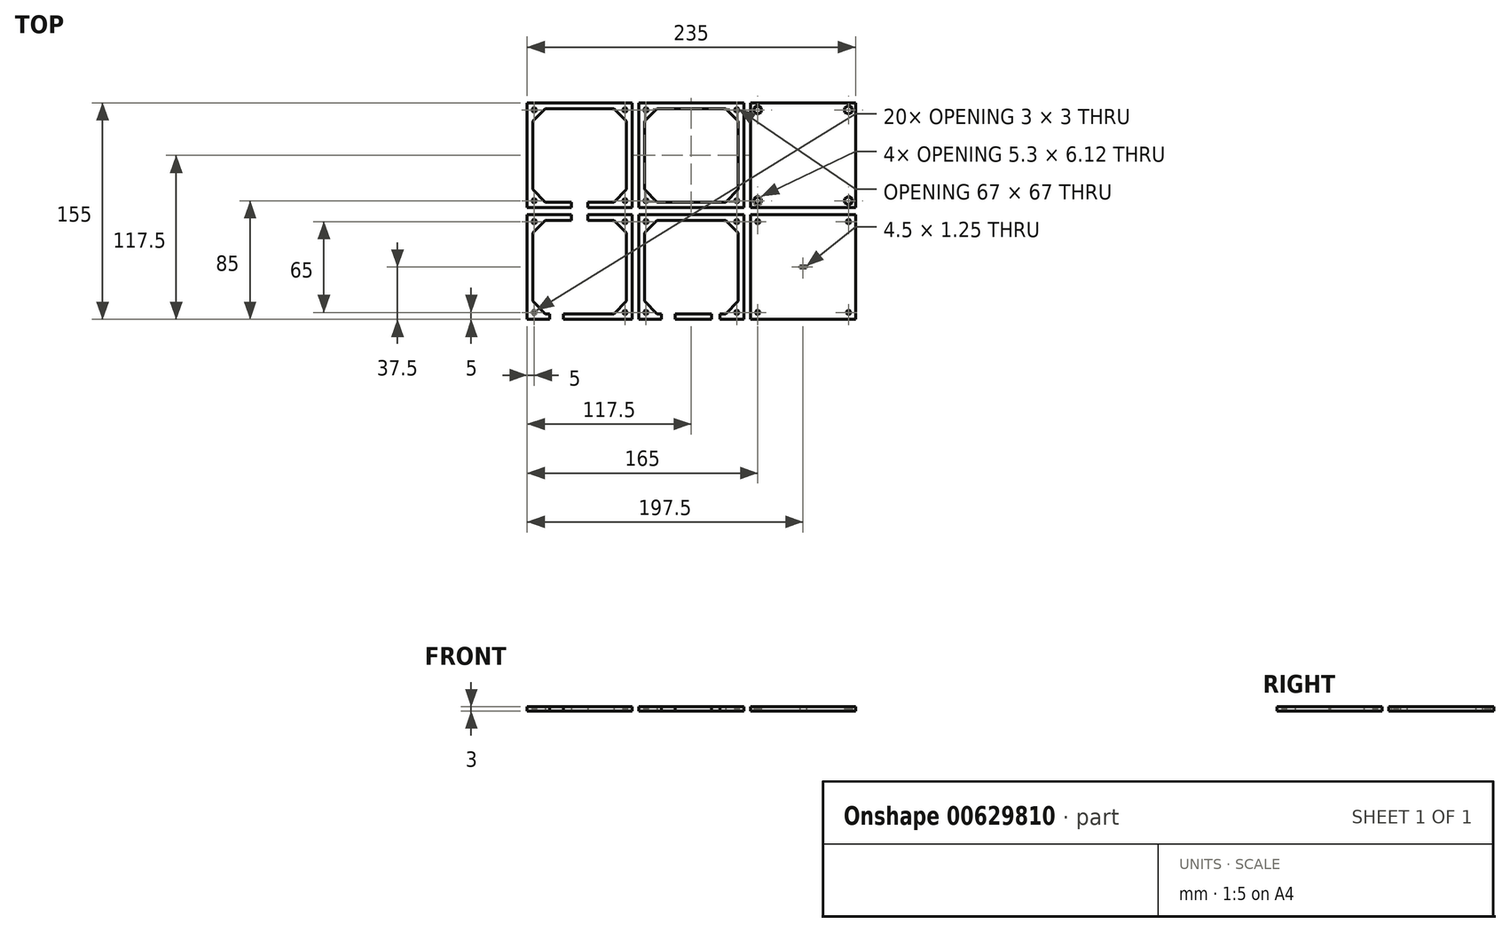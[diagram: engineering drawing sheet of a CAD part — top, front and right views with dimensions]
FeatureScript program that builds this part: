
annotation { "Feature Type Name" : "Feature", "Feature Type Description" : "" }
export const myFeature = defineFeature(function(context is Context, id is Id, definition is map)
    precondition{}
    {
        {
            var Q0;
            Q0=qCreatedBy(makeId("Top.planeOp"),FACE);
            var sketch = newSketch(context, id + "F0", { "sketchPlane" : qUnion([Q0])});
            skLineSegment(sketch, "E0", {"start": v(-111.29, 73.38) * mm, "end": v(-111.62, 73.71) * mm});
            skLineSegment(sketch, "E1", {"start": v(-111.62, 73.71) * mm, "end": v(-112.04, 73.93) * mm});
            skLineSegment(sketch, "E2", {"start": v(-112.04, 73.93) * mm, "end": v(-112.5, 74) * mm});
            skLineSegment(sketch, "E3", {"start": v(-112.5, 74) * mm, "end": v(-112.96, 73.93) * mm});
            skLineSegment(sketch, "E4", {"start": v(-112.96, 73.93) * mm, "end": v(-113.38, 73.71) * mm});
            skLineSegment(sketch, "E5", {"start": v(-113.38, 73.71) * mm, "end": v(-113.71, 73.38) * mm});
            skLineSegment(sketch, "E6", {"start": v(-113.71, 73.38) * mm, "end": v(-113.93, 72.96) * mm});
            skLineSegment(sketch, "E7", {"start": v(-113.93, 72.96) * mm, "end": v(-114, 72.5) * mm});
            skLineSegment(sketch, "E8", {"start": v(-114, 72.5) * mm, "end": v(-113.93, 72.04) * mm});
            skLineSegment(sketch, "E9", {"start": v(-113.93, 72.04) * mm, "end": v(-113.71, 71.62) * mm});
            skLineSegment(sketch, "E10", {"start": v(-113.71, 71.62) * mm, "end": v(-113.38, 71.29) * mm});
            skLineSegment(sketch, "E11", {"start": v(-113.38, 71.29) * mm, "end": v(-112.96, 71.07) * mm});
            skLineSegment(sketch, "E12", {"start": v(-112.96, 71.07) * mm, "end": v(-112.5, 71) * mm});
            skLineSegment(sketch, "E13", {"start": v(-112.5, 71) * mm, "end": v(-112.04, 71.07) * mm});
            skLineSegment(sketch, "E14", {"start": v(-112.04, 71.07) * mm, "end": v(-111.62, 71.29) * mm});
            skLineSegment(sketch, "E15", {"start": v(-111.62, 71.29) * mm, "end": v(-111.29, 71.62) * mm});
            skLineSegment(sketch, "E16", {"start": v(-111.29, 71.62) * mm, "end": v(-111.07, 72.04) * mm});
            skLineSegment(sketch, "E17", {"start": v(-111.07, 72.04) * mm, "end": v(-111, 72.5) * mm});
            skLineSegment(sketch, "E18", {"start": v(-111, 72.5) * mm, "end": v(-111.07, 72.96) * mm});
            skLineSegment(sketch, "E19", {"start": v(-46.07, 72.96) * mm, "end": v(-46.29, 73.38) * mm});
            skLineSegment(sketch, "E20", {"start": v(-46.29, 73.38) * mm, "end": v(-46.62, 73.71) * mm});
            skLineSegment(sketch, "E21", {"start": v(-46.62, 73.71) * mm, "end": v(-47.04, 73.93) * mm});
            skLineSegment(sketch, "E22", {"start": v(-47.04, 73.93) * mm, "end": v(-47.5, 74) * mm});
            skLineSegment(sketch, "E23", {"start": v(-47.5, 74) * mm, "end": v(-47.96, 73.93) * mm});
            skLineSegment(sketch, "E24", {"start": v(-47.96, 73.93) * mm, "end": v(-48.38, 73.71) * mm});
            skLineSegment(sketch, "E25", {"start": v(-48.38, 73.71) * mm, "end": v(-48.71, 73.38) * mm});
            skLineSegment(sketch, "E26", {"start": v(-48.71, 73.38) * mm, "end": v(-48.93, 72.96) * mm});
            skLineSegment(sketch, "E27", {"start": v(-48.93, 72.96) * mm, "end": v(-49, 72.5) * mm});
            skLineSegment(sketch, "E28", {"start": v(-49, 72.5) * mm, "end": v(-48.93, 72.04) * mm});
            skLineSegment(sketch, "E29", {"start": v(-48.93, 72.04) * mm, "end": v(-48.71, 71.62) * mm});
            skLineSegment(sketch, "E30", {"start": v(-48.71, 71.62) * mm, "end": v(-48.38, 71.29) * mm});
            skLineSegment(sketch, "E31", {"start": v(-48.38, 71.29) * mm, "end": v(-47.96, 71.07) * mm});
            skLineSegment(sketch, "E32", {"start": v(-47.96, 71.07) * mm, "end": v(-47.5, 71) * mm});
            skLineSegment(sketch, "E33", {"start": v(-47.5, 71) * mm, "end": v(-47.04, 71.07) * mm});
            skLineSegment(sketch, "E34", {"start": v(-47.04, 71.07) * mm, "end": v(-46.62, 71.29) * mm});
            skLineSegment(sketch, "E35", {"start": v(-46.62, 71.29) * mm, "end": v(-46.29, 71.62) * mm});
            skLineSegment(sketch, "E36", {"start": v(-46.29, 71.62) * mm, "end": v(-46.07, 72.04) * mm});
            skLineSegment(sketch, "E37", {"start": v(-46.07, 72.04) * mm, "end": v(-46, 72.5) * mm});
            skLineSegment(sketch, "E38", {"start": v(-46, 72.5) * mm, "end": v(-46.07, 72.96) * mm});
            skLineSegment(sketch, "E39", {"start": v(-46.07, 7.96) * mm, "end": v(-46.29, 8.38) * mm});
            skLineSegment(sketch, "E40", {"start": v(-46.29, 8.38) * mm, "end": v(-46.62, 8.71) * mm});
            skLineSegment(sketch, "E41", {"start": v(-46.62, 8.71) * mm, "end": v(-47.04, 8.93) * mm});
            skLineSegment(sketch, "E42", {"start": v(-47.04, 8.93) * mm, "end": v(-47.5, 9) * mm});
            skLineSegment(sketch, "E43", {"start": v(-47.5, 9) * mm, "end": v(-47.96, 8.93) * mm});
            skLineSegment(sketch, "E44", {"start": v(-47.96, 8.93) * mm, "end": v(-48.38, 8.71) * mm});
            skLineSegment(sketch, "E45", {"start": v(-48.38, 8.71) * mm, "end": v(-48.71, 8.38) * mm});
            skLineSegment(sketch, "E46", {"start": v(-48.71, 8.38) * mm, "end": v(-48.93, 7.96) * mm});
            skLineSegment(sketch, "E47", {"start": v(-48.93, 7.96) * mm, "end": v(-49, 7.5) * mm});
            skLineSegment(sketch, "E48", {"start": v(-49, 7.5) * mm, "end": v(-48.93, 7.04) * mm});
            skLineSegment(sketch, "E49", {"start": v(-48.93, 7.04) * mm, "end": v(-48.71, 6.62) * mm});
            skLineSegment(sketch, "E50", {"start": v(-48.71, 6.62) * mm, "end": v(-48.38, 6.29) * mm});
            skLineSegment(sketch, "E51", {"start": v(-48.38, 6.29) * mm, "end": v(-47.96, 6.07) * mm});
            skLineSegment(sketch, "E52", {"start": v(-47.96, 6.07) * mm, "end": v(-47.5, 6) * mm});
            skLineSegment(sketch, "E53", {"start": v(-47.5, 6) * mm, "end": v(-47.04, 6.07) * mm});
            skLineSegment(sketch, "E54", {"start": v(-47.04, 6.07) * mm, "end": v(-46.62, 6.29) * mm});
            skLineSegment(sketch, "E55", {"start": v(-46.62, 6.29) * mm, "end": v(-46.29, 6.62) * mm});
            skLineSegment(sketch, "E56", {"start": v(-46.29, 6.62) * mm, "end": v(-46.07, 7.04) * mm});
            skLineSegment(sketch, "E57", {"start": v(-46.07, 7.04) * mm, "end": v(-46, 7.5) * mm});
            skLineSegment(sketch, "E58", {"start": v(-46, 7.5) * mm, "end": v(-46.07, 7.96) * mm});
            skLineSegment(sketch, "E59", {"start": v(-111.07, 7.96) * mm, "end": v(-111.29, 8.38) * mm});
            skLineSegment(sketch, "E60", {"start": v(-111.29, 8.38) * mm, "end": v(-111.62, 8.71) * mm});
            skLineSegment(sketch, "E61", {"start": v(-111.62, 8.71) * mm, "end": v(-112.04, 8.93) * mm});
            skLineSegment(sketch, "E62", {"start": v(-112.04, 8.93) * mm, "end": v(-112.5, 9) * mm});
            skLineSegment(sketch, "E63", {"start": v(-112.5, 9) * mm, "end": v(-112.96, 8.93) * mm});
            skLineSegment(sketch, "E64", {"start": v(-112.96, 8.93) * mm, "end": v(-113.38, 8.71) * mm});
            skLineSegment(sketch, "E65", {"start": v(-113.38, 8.71) * mm, "end": v(-113.71, 8.38) * mm});
            skLineSegment(sketch, "E66", {"start": v(-113.71, 8.38) * mm, "end": v(-113.93, 7.96) * mm});
            skLineSegment(sketch, "E67", {"start": v(-113.93, 7.96) * mm, "end": v(-114, 7.5) * mm});
            skLineSegment(sketch, "E68", {"start": v(-114, 7.5) * mm, "end": v(-113.93, 7.04) * mm});
            skLineSegment(sketch, "E69", {"start": v(-113.93, 7.04) * mm, "end": v(-113.71, 6.62) * mm});
            skLineSegment(sketch, "E70", {"start": v(-113.71, 6.62) * mm, "end": v(-113.38, 6.29) * mm});
            skLineSegment(sketch, "E71", {"start": v(-113.38, 6.29) * mm, "end": v(-112.96, 6.07) * mm});
            skLineSegment(sketch, "E72", {"start": v(-112.96, 6.07) * mm, "end": v(-112.5, 6) * mm});
            skLineSegment(sketch, "E73", {"start": v(-112.5, 6) * mm, "end": v(-112.04, 6.07) * mm});
            skLineSegment(sketch, "E74", {"start": v(-112.04, 6.07) * mm, "end": v(-111.62, 6.29) * mm});
            skLineSegment(sketch, "E75", {"start": v(-111.62, 6.29) * mm, "end": v(-111.29, 6.62) * mm});
            skLineSegment(sketch, "E76", {"start": v(-111.29, 6.62) * mm, "end": v(-111.07, 7.04) * mm});
            skLineSegment(sketch, "E77", {"start": v(-111.07, 7.04) * mm, "end": v(-111, 7.5) * mm});
            skLineSegment(sketch, "E78", {"start": v(-111, 7.5) * mm, "end": v(-111.07, 7.96) * mm});
            skLineSegment(sketch, "E79", {"start": v(-55.5, 6.5) * mm, "end": v(-74, 6.5) * mm});
            skLineSegment(sketch, "E80", {"start": v(-86, 6.5) * mm, "end": v(-104.5, 6.5) * mm});
            skLineSegment(sketch, "E81", {"start": v(-46.5, 64.5) * mm, "end": v(-46.5, 15.5) * mm});
            skLineSegment(sketch, "E82", {"start": v(-104.5, 73.5) * mm, "end": v(-55.5, 73.5) * mm});
            skLineSegment(sketch, "E83", {"start": v(-113.5, 15.5) * mm, "end": v(-113.5, 64.5) * mm});
            skLineSegment(sketch, "E84", {"start": v(-31.07, 72.96) * mm, "end": v(-31.29, 73.38) * mm});
            skLineSegment(sketch, "E85", {"start": v(-31.29, 73.38) * mm, "end": v(-31.62, 73.71) * mm});
            skLineSegment(sketch, "E86", {"start": v(-31.62, 73.71) * mm, "end": v(-32.04, 73.93) * mm});
            skLineSegment(sketch, "E87", {"start": v(-32.04, 73.93) * mm, "end": v(-32.5, 74) * mm});
            skLineSegment(sketch, "E88", {"start": v(-32.5, 74) * mm, "end": v(-32.96, 73.93) * mm});
            skLineSegment(sketch, "E89", {"start": v(-32.96, 73.93) * mm, "end": v(-33.38, 73.71) * mm});
            skLineSegment(sketch, "E90", {"start": v(-33.38, 73.71) * mm, "end": v(-33.71, 73.38) * mm});
            skLineSegment(sketch, "E91", {"start": v(-33.71, 73.38) * mm, "end": v(-33.93, 72.96) * mm});
            skLineSegment(sketch, "E92", {"start": v(-33.93, 72.96) * mm, "end": v(-34, 72.5) * mm});
            skLineSegment(sketch, "E93", {"start": v(-34, 72.5) * mm, "end": v(-33.93, 72.04) * mm});
            skLineSegment(sketch, "E94", {"start": v(-33.93, 72.04) * mm, "end": v(-33.71, 71.62) * mm});
            skLineSegment(sketch, "E95", {"start": v(-33.71, 71.62) * mm, "end": v(-33.38, 71.29) * mm});
            skLineSegment(sketch, "E96", {"start": v(-33.38, 71.29) * mm, "end": v(-32.96, 71.07) * mm});
            skLineSegment(sketch, "E97", {"start": v(-32.96, 71.07) * mm, "end": v(-32.5, 71) * mm});
            skLineSegment(sketch, "E98", {"start": v(-32.5, 71) * mm, "end": v(-32.04, 71.07) * mm});
            skLineSegment(sketch, "E99", {"start": v(-32.04, 71.07) * mm, "end": v(-31.62, 71.29) * mm});
            skLineSegment(sketch, "E100", {"start": v(-31.62, 71.29) * mm, "end": v(-31.29, 71.62) * mm});
            skLineSegment(sketch, "E101", {"start": v(-31.29, 71.62) * mm, "end": v(-31.07, 72.04) * mm});
            skLineSegment(sketch, "E102", {"start": v(-31.07, 72.04) * mm, "end": v(-31, 72.5) * mm});
            skLineSegment(sketch, "E103", {"start": v(-31, 72.5) * mm, "end": v(-31.07, 72.96) * mm});
            skLineSegment(sketch, "E104", {"start": v(33.93, 72.96) * mm, "end": v(33.71, 73.38) * mm});
            skLineSegment(sketch, "E105", {"start": v(33.71, 73.38) * mm, "end": v(33.38, 73.71) * mm});
            skLineSegment(sketch, "E106", {"start": v(33.38, 73.71) * mm, "end": v(32.96, 73.93) * mm});
            skLineSegment(sketch, "E107", {"start": v(32.96, 73.93) * mm, "end": v(32.5, 74) * mm});
            skLineSegment(sketch, "E108", {"start": v(32.5, 74) * mm, "end": v(32.04, 73.93) * mm});
            skLineSegment(sketch, "E109", {"start": v(32.04, 73.93) * mm, "end": v(31.62, 73.71) * mm});
            skLineSegment(sketch, "E110", {"start": v(31.62, 73.71) * mm, "end": v(31.29, 73.38) * mm});
            skLineSegment(sketch, "E111", {"start": v(31.29, 73.38) * mm, "end": v(31.07, 72.96) * mm});
            skLineSegment(sketch, "E112", {"start": v(31.07, 72.96) * mm, "end": v(31, 72.5) * mm});
            skLineSegment(sketch, "E113", {"start": v(31, 72.5) * mm, "end": v(31.07, 72.04) * mm});
            skLineSegment(sketch, "E114", {"start": v(31.07, 72.04) * mm, "end": v(31.29, 71.62) * mm});
            skLineSegment(sketch, "E115", {"start": v(31.29, 71.62) * mm, "end": v(31.62, 71.29) * mm});
            skLineSegment(sketch, "E116", {"start": v(31.62, 71.29) * mm, "end": v(32.04, 71.07) * mm});
            skLineSegment(sketch, "E117", {"start": v(32.04, 71.07) * mm, "end": v(32.5, 71) * mm});
            skLineSegment(sketch, "E118", {"start": v(32.5, 71) * mm, "end": v(32.96, 71.07) * mm});
            skLineSegment(sketch, "E119", {"start": v(32.96, 71.07) * mm, "end": v(33.38, 71.29) * mm});
            skLineSegment(sketch, "E120", {"start": v(33.38, 71.29) * mm, "end": v(33.71, 71.62) * mm});
            skLineSegment(sketch, "E121", {"start": v(33.71, 71.62) * mm, "end": v(33.93, 72.04) * mm});
            skLineSegment(sketch, "E122", {"start": v(33.93, 72.04) * mm, "end": v(34, 72.5) * mm});
            skLineSegment(sketch, "E123", {"start": v(34, 72.5) * mm, "end": v(33.93, 72.96) * mm});
            skLineSegment(sketch, "E124", {"start": v(33.93, 7.96) * mm, "end": v(33.71, 8.38) * mm});
            skLineSegment(sketch, "E125", {"start": v(33.71, 8.38) * mm, "end": v(33.38, 8.71) * mm});
            skLineSegment(sketch, "E126", {"start": v(33.38, 8.71) * mm, "end": v(32.96, 8.93) * mm});
            skLineSegment(sketch, "E127", {"start": v(32.96, 8.93) * mm, "end": v(32.5, 9) * mm});
            skLineSegment(sketch, "E128", {"start": v(32.5, 9) * mm, "end": v(32.04, 8.93) * mm});
            skLineSegment(sketch, "E129", {"start": v(32.04, 8.93) * mm, "end": v(31.62, 8.71) * mm});
            skLineSegment(sketch, "E130", {"start": v(31.62, 8.71) * mm, "end": v(31.29, 8.38) * mm});
            skLineSegment(sketch, "E131", {"start": v(31.29, 8.38) * mm, "end": v(31.07, 7.96) * mm});
            skLineSegment(sketch, "E132", {"start": v(31.07, 7.96) * mm, "end": v(31, 7.5) * mm});
            skLineSegment(sketch, "E133", {"start": v(31, 7.5) * mm, "end": v(31.07, 7.04) * mm});
            skLineSegment(sketch, "E134", {"start": v(31.07, 7.04) * mm, "end": v(31.29, 6.62) * mm});
            skLineSegment(sketch, "E135", {"start": v(31.29, 6.62) * mm, "end": v(31.62, 6.29) * mm});
            skLineSegment(sketch, "E136", {"start": v(31.62, 6.29) * mm, "end": v(32.04, 6.07) * mm});
            skLineSegment(sketch, "E137", {"start": v(32.04, 6.07) * mm, "end": v(32.5, 6) * mm});
            skLineSegment(sketch, "E138", {"start": v(32.5, 6) * mm, "end": v(32.96, 6.07) * mm});
            skLineSegment(sketch, "E139", {"start": v(32.96, 6.07) * mm, "end": v(33.38, 6.29) * mm});
            skLineSegment(sketch, "E140", {"start": v(33.38, 6.29) * mm, "end": v(33.71, 6.62) * mm});
            skLineSegment(sketch, "E141", {"start": v(33.71, 6.62) * mm, "end": v(33.93, 7.04) * mm});
            skLineSegment(sketch, "E142", {"start": v(33.93, 7.04) * mm, "end": v(34, 7.5) * mm});
            skLineSegment(sketch, "E143", {"start": v(34, 7.5) * mm, "end": v(33.93, 7.96) * mm});
            skLineSegment(sketch, "E144", {"start": v(-31.07, 7.96) * mm, "end": v(-31.29, 8.38) * mm});
            skLineSegment(sketch, "E145", {"start": v(-31.29, 8.38) * mm, "end": v(-31.62, 8.71) * mm});
            skLineSegment(sketch, "E146", {"start": v(-31.62, 8.71) * mm, "end": v(-32.04, 8.93) * mm});
            skLineSegment(sketch, "E147", {"start": v(-32.04, 8.93) * mm, "end": v(-32.5, 9) * mm});
            skLineSegment(sketch, "E148", {"start": v(-32.5, 9) * mm, "end": v(-32.96, 8.93) * mm});
            skLineSegment(sketch, "E149", {"start": v(-32.96, 8.93) * mm, "end": v(-33.38, 8.71) * mm});
            skLineSegment(sketch, "E150", {"start": v(-33.38, 8.71) * mm, "end": v(-33.71, 8.38) * mm});
            skLineSegment(sketch, "E151", {"start": v(-33.71, 8.38) * mm, "end": v(-33.93, 7.96) * mm});
            skLineSegment(sketch, "E152", {"start": v(-33.93, 7.96) * mm, "end": v(-34, 7.5) * mm});
            skLineSegment(sketch, "E153", {"start": v(-34, 7.5) * mm, "end": v(-33.93, 7.04) * mm});
            skLineSegment(sketch, "E154", {"start": v(-33.93, 7.04) * mm, "end": v(-33.71, 6.62) * mm});
            skLineSegment(sketch, "E155", {"start": v(-33.71, 6.62) * mm, "end": v(-33.38, 6.29) * mm});
            skLineSegment(sketch, "E156", {"start": v(-33.38, 6.29) * mm, "end": v(-32.96, 6.07) * mm});
            skLineSegment(sketch, "E157", {"start": v(-32.96, 6.07) * mm, "end": v(-32.5, 6) * mm});
            skLineSegment(sketch, "E158", {"start": v(-32.5, 6) * mm, "end": v(-32.04, 6.07) * mm});
            skLineSegment(sketch, "E159", {"start": v(-32.04, 6.07) * mm, "end": v(-31.62, 6.29) * mm});
            skLineSegment(sketch, "E160", {"start": v(-31.62, 6.29) * mm, "end": v(-31.29, 6.62) * mm});
            skLineSegment(sketch, "E161", {"start": v(-31.29, 6.62) * mm, "end": v(-31.07, 7.04) * mm});
            skLineSegment(sketch, "E162", {"start": v(-31.07, 7.04) * mm, "end": v(-31, 7.5) * mm});
            skLineSegment(sketch, "E163", {"start": v(-31, 7.5) * mm, "end": v(-31.07, 7.96) * mm});
            skLineSegment(sketch, "E164", {"start": v(24.5, 6.5) * mm, "end": v(-24.5, 6.5) * mm});
            skLineSegment(sketch, "E165", {"start": v(33.5, 64.5) * mm, "end": v(33.5, 15.5) * mm});
            skLineSegment(sketch, "E166", {"start": v(-33.5, 15.5) * mm, "end": v(-33.5, 64.5) * mm});
            skLineSegment(sketch, "E167", {"start": v(-111.07, -7.04) * mm, "end": v(-111.29, -6.62) * mm});
            skLineSegment(sketch, "E168", {"start": v(-111.29, -6.62) * mm, "end": v(-111.62, -6.29) * mm});
            skLineSegment(sketch, "E169", {"start": v(-111.62, -6.29) * mm, "end": v(-112.04, -6.07) * mm});
            skLineSegment(sketch, "E170", {"start": v(-112.04, -6.07) * mm, "end": v(-112.5, -6) * mm});
            skLineSegment(sketch, "E171", {"start": v(-112.5, -6) * mm, "end": v(-112.96, -6.07) * mm});
            skLineSegment(sketch, "E172", {"start": v(-112.96, -6.07) * mm, "end": v(-113.38, -6.29) * mm});
            skLineSegment(sketch, "E173", {"start": v(-113.38, -6.29) * mm, "end": v(-113.71, -6.62) * mm});
            skLineSegment(sketch, "E174", {"start": v(-113.71, -6.62) * mm, "end": v(-113.93, -7.04) * mm});
            skLineSegment(sketch, "E175", {"start": v(-113.93, -7.04) * mm, "end": v(-114, -7.5) * mm});
            skLineSegment(sketch, "E176", {"start": v(-114, -7.5) * mm, "end": v(-113.93, -7.96) * mm});
            skLineSegment(sketch, "E177", {"start": v(-113.93, -7.96) * mm, "end": v(-113.71, -8.38) * mm});
            skLineSegment(sketch, "E178", {"start": v(-113.71, -8.38) * mm, "end": v(-113.38, -8.71) * mm});
            skLineSegment(sketch, "E179", {"start": v(-113.38, -8.71) * mm, "end": v(-112.96, -8.93) * mm});
            skLineSegment(sketch, "E180", {"start": v(-112.96, -8.93) * mm, "end": v(-112.5, -9) * mm});
            skLineSegment(sketch, "E181", {"start": v(-112.5, -9) * mm, "end": v(-112.04, -8.93) * mm});
            skLineSegment(sketch, "E182", {"start": v(-112.04, -8.93) * mm, "end": v(-111.62, -8.71) * mm});
            skLineSegment(sketch, "E183", {"start": v(-111.62, -8.71) * mm, "end": v(-111.29, -8.38) * mm});
            skLineSegment(sketch, "E184", {"start": v(-111.29, -8.38) * mm, "end": v(-111.07, -7.96) * mm});
            skLineSegment(sketch, "E185", {"start": v(-111.07, -7.96) * mm, "end": v(-111, -7.5) * mm});
            skLineSegment(sketch, "E186", {"start": v(-111, -7.5) * mm, "end": v(-111.07, -7.04) * mm});
            skLineSegment(sketch, "E187", {"start": v(-46.07, -7.04) * mm, "end": v(-46.29, -6.62) * mm});
            skLineSegment(sketch, "E188", {"start": v(-46.29, -6.62) * mm, "end": v(-46.62, -6.29) * mm});
            skLineSegment(sketch, "E189", {"start": v(-46.62, -6.29) * mm, "end": v(-47.04, -6.07) * mm});
            skLineSegment(sketch, "E190", {"start": v(-47.04, -6.07) * mm, "end": v(-47.5, -6) * mm});
            skLineSegment(sketch, "E191", {"start": v(-47.5, -6) * mm, "end": v(-47.96, -6.07) * mm});
            skLineSegment(sketch, "E192", {"start": v(-47.96, -6.07) * mm, "end": v(-48.38, -6.29) * mm});
            skLineSegment(sketch, "E193", {"start": v(-48.38, -6.29) * mm, "end": v(-48.71, -6.62) * mm});
            skLineSegment(sketch, "E194", {"start": v(-48.71, -6.62) * mm, "end": v(-48.93, -7.04) * mm});
            skLineSegment(sketch, "E195", {"start": v(-48.93, -7.04) * mm, "end": v(-49, -7.5) * mm});
            skLineSegment(sketch, "E196", {"start": v(-49, -7.5) * mm, "end": v(-48.93, -7.96) * mm});
            skLineSegment(sketch, "E197", {"start": v(-48.93, -7.96) * mm, "end": v(-48.71, -8.38) * mm});
            skLineSegment(sketch, "E198", {"start": v(-48.71, -8.38) * mm, "end": v(-48.38, -8.71) * mm});
            skLineSegment(sketch, "E199", {"start": v(-48.38, -8.71) * mm, "end": v(-47.96, -8.93) * mm});
            skLineSegment(sketch, "E200", {"start": v(-47.96, -8.93) * mm, "end": v(-47.5, -9) * mm});
            skLineSegment(sketch, "E201", {"start": v(-47.5, -9) * mm, "end": v(-47.04, -8.93) * mm});
            skLineSegment(sketch, "E202", {"start": v(-47.04, -8.93) * mm, "end": v(-46.62, -8.71) * mm});
            skLineSegment(sketch, "E203", {"start": v(-46.62, -8.71) * mm, "end": v(-46.29, -8.38) * mm});
            skLineSegment(sketch, "E204", {"start": v(-46.29, -8.38) * mm, "end": v(-46.07, -7.96) * mm});
            skLineSegment(sketch, "E205", {"start": v(-46.07, -7.96) * mm, "end": v(-46, -7.5) * mm});
            skLineSegment(sketch, "E206", {"start": v(-46, -7.5) * mm, "end": v(-46.07, -7.04) * mm});
            skLineSegment(sketch, "E207", {"start": v(-46.07, -72.04) * mm, "end": v(-46.29, -71.62) * mm});
            skLineSegment(sketch, "E208", {"start": v(-46.29, -71.62) * mm, "end": v(-46.62, -71.29) * mm});
            skLineSegment(sketch, "E209", {"start": v(-46.62, -71.29) * mm, "end": v(-47.04, -71.07) * mm});
            skLineSegment(sketch, "E210", {"start": v(-47.04, -71.07) * mm, "end": v(-47.5, -71) * mm});
            skLineSegment(sketch, "E211", {"start": v(-47.5, -71) * mm, "end": v(-47.96, -71.07) * mm});
            skLineSegment(sketch, "E212", {"start": v(-47.96, -71.07) * mm, "end": v(-48.38, -71.29) * mm});
            skLineSegment(sketch, "E213", {"start": v(-48.38, -71.29) * mm, "end": v(-48.71, -71.62) * mm});
            skLineSegment(sketch, "E214", {"start": v(-48.71, -71.62) * mm, "end": v(-48.93, -72.04) * mm});
            skLineSegment(sketch, "E215", {"start": v(-48.93, -72.04) * mm, "end": v(-49, -72.5) * mm});
            skLineSegment(sketch, "E216", {"start": v(-49, -72.5) * mm, "end": v(-48.93, -72.96) * mm});
            skLineSegment(sketch, "E217", {"start": v(-48.93, -72.96) * mm, "end": v(-48.71, -73.38) * mm});
            skLineSegment(sketch, "E218", {"start": v(-48.71, -73.38) * mm, "end": v(-48.38, -73.71) * mm});
            skLineSegment(sketch, "E219", {"start": v(-48.38, -73.71) * mm, "end": v(-47.96, -73.93) * mm});
            skLineSegment(sketch, "E220", {"start": v(-47.96, -73.93) * mm, "end": v(-47.5, -74) * mm});
            skLineSegment(sketch, "E221", {"start": v(-47.5, -74) * mm, "end": v(-47.04, -73.93) * mm});
            skLineSegment(sketch, "E222", {"start": v(-47.04, -73.93) * mm, "end": v(-46.62, -73.71) * mm});
            skLineSegment(sketch, "E223", {"start": v(-46.62, -73.71) * mm, "end": v(-46.29, -73.38) * mm});
            skLineSegment(sketch, "E224", {"start": v(-46.29, -73.38) * mm, "end": v(-46.07, -72.96) * mm});
            skLineSegment(sketch, "E225", {"start": v(-46.07, -72.96) * mm, "end": v(-46, -72.5) * mm});
            skLineSegment(sketch, "E226", {"start": v(-46, -72.5) * mm, "end": v(-46.07, -72.04) * mm});
            skLineSegment(sketch, "E227", {"start": v(-111.07, -72.04) * mm, "end": v(-111.29, -71.62) * mm});
            skLineSegment(sketch, "E228", {"start": v(-111.29, -71.62) * mm, "end": v(-111.62, -71.29) * mm});
            skLineSegment(sketch, "E229", {"start": v(-111.62, -71.29) * mm, "end": v(-112.04, -71.07) * mm});
            skLineSegment(sketch, "E230", {"start": v(-112.04, -71.07) * mm, "end": v(-112.5, -71) * mm});
            skLineSegment(sketch, "E231", {"start": v(-112.5, -71) * mm, "end": v(-112.96, -71.07) * mm});
            skLineSegment(sketch, "E232", {"start": v(-112.96, -71.07) * mm, "end": v(-113.38, -71.29) * mm});
            skLineSegment(sketch, "E233", {"start": v(-113.38, -71.29) * mm, "end": v(-113.71, -71.62) * mm});
            skLineSegment(sketch, "E234", {"start": v(-113.71, -71.62) * mm, "end": v(-113.93, -72.04) * mm});
            skLineSegment(sketch, "E235", {"start": v(-113.93, -72.04) * mm, "end": v(-114, -72.5) * mm});
            skLineSegment(sketch, "E236", {"start": v(-114, -72.5) * mm, "end": v(-113.93, -72.96) * mm});
            skLineSegment(sketch, "E237", {"start": v(-113.93, -72.96) * mm, "end": v(-113.71, -73.38) * mm});
            skLineSegment(sketch, "E238", {"start": v(-113.71, -73.38) * mm, "end": v(-113.38, -73.71) * mm});
            skLineSegment(sketch, "E239", {"start": v(-113.38, -73.71) * mm, "end": v(-112.96, -73.93) * mm});
            skLineSegment(sketch, "E240", {"start": v(-112.96, -73.93) * mm, "end": v(-112.5, -74) * mm});
            skLineSegment(sketch, "E241", {"start": v(-112.5, -74) * mm, "end": v(-112.04, -73.93) * mm});
            skLineSegment(sketch, "E242", {"start": v(-112.04, -73.93) * mm, "end": v(-111.62, -73.71) * mm});
            skLineSegment(sketch, "E243", {"start": v(-111.62, -73.71) * mm, "end": v(-111.29, -73.38) * mm});
            skLineSegment(sketch, "E244", {"start": v(-111.29, -73.38) * mm, "end": v(-111.07, -72.96) * mm});
            skLineSegment(sketch, "E245", {"start": v(-111.07, -72.96) * mm, "end": v(-111, -72.5) * mm});
            skLineSegment(sketch, "E246", {"start": v(-111, -72.5) * mm, "end": v(-111.07, -72.04) * mm});
            skLineSegment(sketch, "E247", {"start": v(-101.5, -73.5) * mm, "end": v(-104.5, -73.5) * mm});
            skLineSegment(sketch, "E248", {"start": v(-55.5, -73.5) * mm, "end": v(-91.5, -73.5) * mm});
            skLineSegment(sketch, "E249", {"start": v(-46.5, -15.5) * mm, "end": v(-46.5, -64.5) * mm});
            skLineSegment(sketch, "E250", {"start": v(-74, -6.5) * mm, "end": v(-55.5, -6.5) * mm});
            skLineSegment(sketch, "E251", {"start": v(-104.5, -6.5) * mm, "end": v(-86, -6.5) * mm});
            skLineSegment(sketch, "E252", {"start": v(-113.5, -64.5) * mm, "end": v(-113.5, -15.5) * mm});
            skLineSegment(sketch, "E253", {"start": v(-31.07, -7.04) * mm, "end": v(-31.29, -6.62) * mm});
            skLineSegment(sketch, "E254", {"start": v(-31.29, -6.62) * mm, "end": v(-31.62, -6.29) * mm});
            skLineSegment(sketch, "E255", {"start": v(-31.62, -6.29) * mm, "end": v(-32.04, -6.07) * mm});
            skLineSegment(sketch, "E256", {"start": v(-32.04, -6.07) * mm, "end": v(-32.5, -6) * mm});
            skLineSegment(sketch, "E257", {"start": v(-32.5, -6) * mm, "end": v(-32.96, -6.07) * mm});
            skLineSegment(sketch, "E258", {"start": v(-32.96, -6.07) * mm, "end": v(-33.38, -6.29) * mm});
            skLineSegment(sketch, "E259", {"start": v(-33.38, -6.29) * mm, "end": v(-33.71, -6.62) * mm});
            skLineSegment(sketch, "E260", {"start": v(-33.71, -6.62) * mm, "end": v(-33.93, -7.04) * mm});
            skLineSegment(sketch, "E261", {"start": v(-33.93, -7.04) * mm, "end": v(-34, -7.5) * mm});
            skLineSegment(sketch, "E262", {"start": v(-34, -7.5) * mm, "end": v(-33.93, -7.96) * mm});
            skLineSegment(sketch, "E263", {"start": v(-33.93, -7.96) * mm, "end": v(-33.71, -8.38) * mm});
            skLineSegment(sketch, "E264", {"start": v(-33.71, -8.38) * mm, "end": v(-33.38, -8.71) * mm});
            skLineSegment(sketch, "E265", {"start": v(-33.38, -8.71) * mm, "end": v(-32.96, -8.93) * mm});
            skLineSegment(sketch, "E266", {"start": v(-32.96, -8.93) * mm, "end": v(-32.5, -9) * mm});
            skLineSegment(sketch, "E267", {"start": v(-32.5, -9) * mm, "end": v(-32.04, -8.93) * mm});
            skLineSegment(sketch, "E268", {"start": v(-32.04, -8.93) * mm, "end": v(-31.62, -8.71) * mm});
            skLineSegment(sketch, "E269", {"start": v(-31.62, -8.71) * mm, "end": v(-31.29, -8.38) * mm});
            skLineSegment(sketch, "E270", {"start": v(-31.29, -8.38) * mm, "end": v(-31.07, -7.96) * mm});
            skLineSegment(sketch, "E271", {"start": v(-31.07, -7.96) * mm, "end": v(-31, -7.5) * mm});
            skLineSegment(sketch, "E272", {"start": v(-31, -7.5) * mm, "end": v(-31.07, -7.04) * mm});
            skLineSegment(sketch, "E273", {"start": v(33.93, -7.04) * mm, "end": v(33.71, -6.62) * mm});
            skLineSegment(sketch, "E274", {"start": v(33.71, -6.62) * mm, "end": v(33.38, -6.29) * mm});
            skLineSegment(sketch, "E275", {"start": v(33.38, -6.29) * mm, "end": v(32.96, -6.07) * mm});
            skLineSegment(sketch, "E276", {"start": v(32.96, -6.07) * mm, "end": v(32.5, -6) * mm});
            skLineSegment(sketch, "E277", {"start": v(32.5, -6) * mm, "end": v(32.04, -6.07) * mm});
            skLineSegment(sketch, "E278", {"start": v(32.04, -6.07) * mm, "end": v(31.62, -6.29) * mm});
            skLineSegment(sketch, "E279", {"start": v(31.62, -6.29) * mm, "end": v(31.29, -6.62) * mm});
            skLineSegment(sketch, "E280", {"start": v(31.29, -6.62) * mm, "end": v(31.07, -7.04) * mm});
            skLineSegment(sketch, "E281", {"start": v(31.07, -7.04) * mm, "end": v(31, -7.5) * mm});
            skLineSegment(sketch, "E282", {"start": v(31, -7.5) * mm, "end": v(31.07, -7.96) * mm});
            skLineSegment(sketch, "E283", {"start": v(31.07, -7.96) * mm, "end": v(31.29, -8.38) * mm});
            skLineSegment(sketch, "E284", {"start": v(31.29, -8.38) * mm, "end": v(31.62, -8.71) * mm});
            skLineSegment(sketch, "E285", {"start": v(31.62, -8.71) * mm, "end": v(32.04, -8.93) * mm});
            skLineSegment(sketch, "E286", {"start": v(32.04, -8.93) * mm, "end": v(32.5, -9) * mm});
            skLineSegment(sketch, "E287", {"start": v(32.5, -9) * mm, "end": v(32.96, -8.93) * mm});
            skLineSegment(sketch, "E288", {"start": v(32.96, -8.93) * mm, "end": v(33.38, -8.71) * mm});
            skLineSegment(sketch, "E289", {"start": v(33.38, -8.71) * mm, "end": v(33.71, -8.38) * mm});
            skLineSegment(sketch, "E290", {"start": v(33.71, -8.38) * mm, "end": v(33.93, -7.96) * mm});
            skLineSegment(sketch, "E291", {"start": v(33.93, -7.96) * mm, "end": v(34, -7.5) * mm});
            skLineSegment(sketch, "E292", {"start": v(34, -7.5) * mm, "end": v(33.93, -7.04) * mm});
            skLineSegment(sketch, "E293", {"start": v(33.93, -72.04) * mm, "end": v(33.71, -71.62) * mm});
            skLineSegment(sketch, "E294", {"start": v(33.71, -71.62) * mm, "end": v(33.38, -71.29) * mm});
            skLineSegment(sketch, "E295", {"start": v(33.38, -71.29) * mm, "end": v(32.96, -71.07) * mm});
            skLineSegment(sketch, "E296", {"start": v(32.96, -71.07) * mm, "end": v(32.5, -71) * mm});
            skLineSegment(sketch, "E297", {"start": v(32.5, -71) * mm, "end": v(32.04, -71.07) * mm});
            skLineSegment(sketch, "E298", {"start": v(32.04, -71.07) * mm, "end": v(31.62, -71.29) * mm});
            skLineSegment(sketch, "E299", {"start": v(31.62, -71.29) * mm, "end": v(31.29, -71.62) * mm});
            skLineSegment(sketch, "E300", {"start": v(31.29, -71.62) * mm, "end": v(31.07, -72.04) * mm});
            skLineSegment(sketch, "E301", {"start": v(31.07, -72.04) * mm, "end": v(31, -72.5) * mm});
            skLineSegment(sketch, "E302", {"start": v(31, -72.5) * mm, "end": v(31.07, -72.96) * mm});
            skLineSegment(sketch, "E303", {"start": v(31.07, -72.96) * mm, "end": v(31.29, -73.38) * mm});
            skLineSegment(sketch, "E304", {"start": v(31.29, -73.38) * mm, "end": v(31.62, -73.71) * mm});
            skLineSegment(sketch, "E305", {"start": v(31.62, -73.71) * mm, "end": v(32.04, -73.93) * mm});
            skLineSegment(sketch, "E306", {"start": v(32.04, -73.93) * mm, "end": v(32.5, -74) * mm});
            skLineSegment(sketch, "E307", {"start": v(32.5, -74) * mm, "end": v(32.96, -73.93) * mm});
            skLineSegment(sketch, "E308", {"start": v(32.96, -73.93) * mm, "end": v(33.38, -73.71) * mm});
            skLineSegment(sketch, "E309", {"start": v(33.38, -73.71) * mm, "end": v(33.71, -73.38) * mm});
            skLineSegment(sketch, "E310", {"start": v(33.71, -73.38) * mm, "end": v(33.93, -72.96) * mm});
            skLineSegment(sketch, "E311", {"start": v(33.93, -72.96) * mm, "end": v(34, -72.5) * mm});
            skLineSegment(sketch, "E312", {"start": v(34, -72.5) * mm, "end": v(33.93, -72.04) * mm});
            skLineSegment(sketch, "E313", {"start": v(-31.07, -72.04) * mm, "end": v(-31.29, -71.62) * mm});
            skLineSegment(sketch, "E314", {"start": v(-31.29, -71.62) * mm, "end": v(-31.62, -71.29) * mm});
            skLineSegment(sketch, "E315", {"start": v(-31.62, -71.29) * mm, "end": v(-32.04, -71.07) * mm});
            skLineSegment(sketch, "E316", {"start": v(-32.04, -71.07) * mm, "end": v(-32.5, -71) * mm});
            skLineSegment(sketch, "E317", {"start": v(-32.5, -71) * mm, "end": v(-32.96, -71.07) * mm});
            skLineSegment(sketch, "E318", {"start": v(-32.96, -71.07) * mm, "end": v(-33.38, -71.29) * mm});
            skLineSegment(sketch, "E319", {"start": v(-33.38, -71.29) * mm, "end": v(-33.71, -71.62) * mm});
            skLineSegment(sketch, "E320", {"start": v(-33.71, -71.62) * mm, "end": v(-33.93, -72.04) * mm});
            skLineSegment(sketch, "E321", {"start": v(-33.93, -72.04) * mm, "end": v(-34, -72.5) * mm});
            skLineSegment(sketch, "E322", {"start": v(-34, -72.5) * mm, "end": v(-33.93, -72.96) * mm});
            skLineSegment(sketch, "E323", {"start": v(-33.93, -72.96) * mm, "end": v(-33.71, -73.38) * mm});
            skLineSegment(sketch, "E324", {"start": v(-33.71, -73.38) * mm, "end": v(-33.38, -73.71) * mm});
            skLineSegment(sketch, "E325", {"start": v(-33.38, -73.71) * mm, "end": v(-32.96, -73.93) * mm});
            skLineSegment(sketch, "E326", {"start": v(-32.96, -73.93) * mm, "end": v(-32.5, -74) * mm});
            skLineSegment(sketch, "E327", {"start": v(-32.5, -74) * mm, "end": v(-32.04, -73.93) * mm});
            skLineSegment(sketch, "E328", {"start": v(-32.04, -73.93) * mm, "end": v(-31.62, -73.71) * mm});
            skLineSegment(sketch, "E329", {"start": v(-31.62, -73.71) * mm, "end": v(-31.29, -73.38) * mm});
            skLineSegment(sketch, "E330", {"start": v(-31.29, -73.38) * mm, "end": v(-31.07, -72.96) * mm});
            skLineSegment(sketch, "E331", {"start": v(-31.07, -72.96) * mm, "end": v(-31, -72.5) * mm});
            skLineSegment(sketch, "E332", {"start": v(-31, -72.5) * mm, "end": v(-31.07, -72.04) * mm});
            skLineSegment(sketch, "E333", {"start": v(33.5, -15.5) * mm, "end": v(33.5, -64.5) * mm});
            skLineSegment(sketch, "E334", {"start": v(-24.5, -6.5) * mm, "end": v(24.5, -6.5) * mm});
            skLineSegment(sketch, "E335", {"start": v(-33.5, -64.5) * mm, "end": v(-33.5, -15.5) * mm});
            skLineSegment(sketch, "E336", {"start": v(48.93, -7.04) * mm, "end": v(48.71, -6.62) * mm});
            skLineSegment(sketch, "E337", {"start": v(48.71, -6.62) * mm, "end": v(48.38, -6.29) * mm});
            skLineSegment(sketch, "E338", {"start": v(48.38, -6.29) * mm, "end": v(47.96, -6.07) * mm});
            skLineSegment(sketch, "E339", {"start": v(47.96, -6.07) * mm, "end": v(47.5, -6) * mm});
            skLineSegment(sketch, "E340", {"start": v(47.5, -6) * mm, "end": v(47.04, -6.07) * mm});
            skLineSegment(sketch, "E341", {"start": v(47.04, -6.07) * mm, "end": v(46.62, -6.29) * mm});
            skLineSegment(sketch, "E342", {"start": v(46.62, -6.29) * mm, "end": v(46.29, -6.62) * mm});
            skLineSegment(sketch, "E343", {"start": v(46.29, -6.62) * mm, "end": v(46.07, -7.04) * mm});
            skLineSegment(sketch, "E344", {"start": v(46.07, -7.04) * mm, "end": v(46, -7.5) * mm});
            skLineSegment(sketch, "E345", {"start": v(46, -7.5) * mm, "end": v(46.07, -7.96) * mm});
            skLineSegment(sketch, "E346", {"start": v(46.07, -7.96) * mm, "end": v(46.29, -8.38) * mm});
            skLineSegment(sketch, "E347", {"start": v(46.29, -8.38) * mm, "end": v(46.62, -8.71) * mm});
            skLineSegment(sketch, "E348", {"start": v(46.62, -8.71) * mm, "end": v(47.04, -8.93) * mm});
            skLineSegment(sketch, "E349", {"start": v(47.04, -8.93) * mm, "end": v(47.5, -9) * mm});
            skLineSegment(sketch, "E350", {"start": v(47.5, -9) * mm, "end": v(47.96, -8.93) * mm});
            skLineSegment(sketch, "E351", {"start": v(47.96, -8.93) * mm, "end": v(48.38, -8.71) * mm});
            skLineSegment(sketch, "E352", {"start": v(48.38, -8.71) * mm, "end": v(48.71, -8.38) * mm});
            skLineSegment(sketch, "E353", {"start": v(48.71, -8.38) * mm, "end": v(48.93, -7.96) * mm});
            skLineSegment(sketch, "E354", {"start": v(48.93, -7.96) * mm, "end": v(49, -7.5) * mm});
            skLineSegment(sketch, "E355", {"start": v(49, -7.5) * mm, "end": v(48.93, -7.04) * mm});
            skLineSegment(sketch, "E356", {"start": v(113.93, -7.04) * mm, "end": v(113.71, -6.62) * mm});
            skLineSegment(sketch, "E357", {"start": v(113.71, -6.62) * mm, "end": v(113.38, -6.29) * mm});
            skLineSegment(sketch, "E358", {"start": v(113.38, -6.29) * mm, "end": v(112.96, -6.07) * mm});
            skLineSegment(sketch, "E359", {"start": v(112.96, -6.07) * mm, "end": v(112.5, -6) * mm});
            skLineSegment(sketch, "E360", {"start": v(112.5, -6) * mm, "end": v(112.04, -6.07) * mm});
            skLineSegment(sketch, "E361", {"start": v(112.04, -6.07) * mm, "end": v(111.62, -6.29) * mm});
            skLineSegment(sketch, "E362", {"start": v(111.62, -6.29) * mm, "end": v(111.29, -6.62) * mm});
            skLineSegment(sketch, "E363", {"start": v(111.29, -6.62) * mm, "end": v(111.07, -7.04) * mm});
            skLineSegment(sketch, "E364", {"start": v(111.07, -7.04) * mm, "end": v(111, -7.5) * mm});
            skLineSegment(sketch, "E365", {"start": v(111, -7.5) * mm, "end": v(111.07, -7.96) * mm});
            skLineSegment(sketch, "E366", {"start": v(111.07, -7.96) * mm, "end": v(111.29, -8.38) * mm});
            skLineSegment(sketch, "E367", {"start": v(111.29, -8.38) * mm, "end": v(111.62, -8.71) * mm});
            skLineSegment(sketch, "E368", {"start": v(111.62, -8.71) * mm, "end": v(112.04, -8.93) * mm});
            skLineSegment(sketch, "E369", {"start": v(112.04, -8.93) * mm, "end": v(112.5, -9) * mm});
            skLineSegment(sketch, "E370", {"start": v(112.5, -9) * mm, "end": v(112.96, -8.93) * mm});
            skLineSegment(sketch, "E371", {"start": v(112.96, -8.93) * mm, "end": v(113.38, -8.71) * mm});
            skLineSegment(sketch, "E372", {"start": v(113.38, -8.71) * mm, "end": v(113.71, -8.38) * mm});
            skLineSegment(sketch, "E373", {"start": v(113.71, -8.38) * mm, "end": v(113.93, -7.96) * mm});
            skLineSegment(sketch, "E374", {"start": v(113.93, -7.96) * mm, "end": v(114, -7.5) * mm});
            skLineSegment(sketch, "E375", {"start": v(114, -7.5) * mm, "end": v(113.93, -7.04) * mm});
            skLineSegment(sketch, "E376", {"start": v(113.93, -72.04) * mm, "end": v(113.71, -71.62) * mm});
            skLineSegment(sketch, "E377", {"start": v(113.71, -71.62) * mm, "end": v(113.38, -71.29) * mm});
            skLineSegment(sketch, "E378", {"start": v(113.38, -71.29) * mm, "end": v(112.96, -71.07) * mm});
            skLineSegment(sketch, "E379", {"start": v(112.96, -71.07) * mm, "end": v(112.5, -71) * mm});
            skLineSegment(sketch, "E380", {"start": v(112.5, -71) * mm, "end": v(112.04, -71.07) * mm});
            skLineSegment(sketch, "E381", {"start": v(112.04, -71.07) * mm, "end": v(111.62, -71.29) * mm});
            skLineSegment(sketch, "E382", {"start": v(111.62, -71.29) * mm, "end": v(111.29, -71.62) * mm});
            skLineSegment(sketch, "E383", {"start": v(111.29, -71.62) * mm, "end": v(111.07, -72.04) * mm});
            skLineSegment(sketch, "E384", {"start": v(111.07, -72.04) * mm, "end": v(111, -72.5) * mm});
            skLineSegment(sketch, "E385", {"start": v(111, -72.5) * mm, "end": v(111.07, -72.96) * mm});
            skLineSegment(sketch, "E386", {"start": v(111.07, -72.96) * mm, "end": v(111.29, -73.38) * mm});
            skLineSegment(sketch, "E387", {"start": v(111.29, -73.38) * mm, "end": v(111.62, -73.71) * mm});
            skLineSegment(sketch, "E388", {"start": v(111.62, -73.71) * mm, "end": v(112.04, -73.93) * mm});
            skLineSegment(sketch, "E389", {"start": v(112.04, -73.93) * mm, "end": v(112.5, -74) * mm});
            skLineSegment(sketch, "E390", {"start": v(112.5, -74) * mm, "end": v(112.96, -73.93) * mm});
            skLineSegment(sketch, "E391", {"start": v(112.96, -73.93) * mm, "end": v(113.38, -73.71) * mm});
            skLineSegment(sketch, "E392", {"start": v(113.38, -73.71) * mm, "end": v(113.71, -73.38) * mm});
            skLineSegment(sketch, "E393", {"start": v(113.71, -73.38) * mm, "end": v(113.93, -72.96) * mm});
            skLineSegment(sketch, "E394", {"start": v(113.93, -72.96) * mm, "end": v(114, -72.5) * mm});
            skLineSegment(sketch, "E395", {"start": v(114, -72.5) * mm, "end": v(113.93, -72.04) * mm});
            skLineSegment(sketch, "E396", {"start": v(48.93, -72.04) * mm, "end": v(48.71, -71.62) * mm});
            skLineSegment(sketch, "E397", {"start": v(48.71, -71.62) * mm, "end": v(48.38, -71.29) * mm});
            skLineSegment(sketch, "E398", {"start": v(48.38, -71.29) * mm, "end": v(47.96, -71.07) * mm});
            skLineSegment(sketch, "E399", {"start": v(47.96, -71.07) * mm, "end": v(47.5, -71) * mm});
            skLineSegment(sketch, "E400", {"start": v(47.5, -71) * mm, "end": v(47.04, -71.07) * mm});
            skLineSegment(sketch, "E401", {"start": v(47.04, -71.07) * mm, "end": v(46.62, -71.29) * mm});
            skLineSegment(sketch, "E402", {"start": v(46.62, -71.29) * mm, "end": v(46.29, -71.62) * mm});
            skLineSegment(sketch, "E403", {"start": v(46.29, -71.62) * mm, "end": v(46.07, -72.04) * mm});
            skLineSegment(sketch, "E404", {"start": v(46.07, -72.04) * mm, "end": v(46, -72.5) * mm});
            skLineSegment(sketch, "E405", {"start": v(46, -72.5) * mm, "end": v(46.07, -72.96) * mm});
            skLineSegment(sketch, "E406", {"start": v(46.07, -72.96) * mm, "end": v(46.29, -73.38) * mm});
            skLineSegment(sketch, "E407", {"start": v(46.29, -73.38) * mm, "end": v(46.62, -73.71) * mm});
            skLineSegment(sketch, "E408", {"start": v(46.62, -73.71) * mm, "end": v(47.04, -73.93) * mm});
            skLineSegment(sketch, "E409", {"start": v(47.04, -73.93) * mm, "end": v(47.5, -74) * mm});
            skLineSegment(sketch, "E410", {"start": v(47.5, -74) * mm, "end": v(47.96, -73.93) * mm});
            skLineSegment(sketch, "E411", {"start": v(47.96, -73.93) * mm, "end": v(48.38, -73.71) * mm});
            skLineSegment(sketch, "E412", {"start": v(48.38, -73.71) * mm, "end": v(48.71, -73.38) * mm});
            skLineSegment(sketch, "E413", {"start": v(48.71, -73.38) * mm, "end": v(48.93, -72.96) * mm});
            skLineSegment(sketch, "E414", {"start": v(48.93, -72.96) * mm, "end": v(49, -72.5) * mm});
            skLineSegment(sketch, "E415", {"start": v(49, -72.5) * mm, "end": v(48.93, -72.04) * mm});
            skLineSegment(sketch, "E416", {"start": v(47.5, 75.56) * mm, "end": v(44.85, 74.03) * mm});
            skLineSegment(sketch, "E417", {"start": v(44.85, 74.03) * mm, "end": v(44.85, 70.97) * mm});
            skLineSegment(sketch, "E418", {"start": v(44.85, 70.97) * mm, "end": v(47.5, 69.44) * mm});
            skLineSegment(sketch, "E419", {"start": v(47.5, 69.44) * mm, "end": v(50.15, 70.97) * mm});
            skLineSegment(sketch, "E420", {"start": v(50.15, 70.97) * mm, "end": v(50.15, 74.03) * mm});
            skLineSegment(sketch, "E421", {"start": v(50.15, 74.03) * mm, "end": v(47.5, 75.56) * mm});
            skLineSegment(sketch, "E422", {"start": v(112.5, 75.56) * mm, "end": v(109.85, 74.03) * mm});
            skLineSegment(sketch, "E423", {"start": v(109.85, 74.03) * mm, "end": v(109.85, 70.97) * mm});
            skLineSegment(sketch, "E424", {"start": v(109.85, 70.97) * mm, "end": v(112.5, 69.44) * mm});
            skLineSegment(sketch, "E425", {"start": v(112.5, 69.44) * mm, "end": v(115.15, 70.97) * mm});
            skLineSegment(sketch, "E426", {"start": v(115.15, 70.97) * mm, "end": v(115.15, 74.03) * mm});
            skLineSegment(sketch, "E427", {"start": v(115.15, 74.03) * mm, "end": v(112.5, 75.56) * mm});
            skLineSegment(sketch, "E428", {"start": v(112.5, 10.56) * mm, "end": v(109.85, 9.03) * mm});
            skLineSegment(sketch, "E429", {"start": v(109.85, 9.03) * mm, "end": v(109.85, 5.97) * mm});
            skLineSegment(sketch, "E430", {"start": v(109.85, 5.97) * mm, "end": v(112.5, 4.44) * mm});
            skLineSegment(sketch, "E431", {"start": v(112.5, 4.44) * mm, "end": v(115.15, 5.97) * mm});
            skLineSegment(sketch, "E432", {"start": v(115.15, 5.97) * mm, "end": v(115.15, 9.03) * mm});
            skLineSegment(sketch, "E433", {"start": v(115.15, 9.03) * mm, "end": v(112.5, 10.56) * mm});
            skLineSegment(sketch, "E434", {"start": v(47.5, 10.56) * mm, "end": v(44.85, 9.03) * mm});
            skLineSegment(sketch, "E435", {"start": v(44.85, 9.03) * mm, "end": v(44.85, 5.97) * mm});
            skLineSegment(sketch, "E436", {"start": v(44.85, 5.97) * mm, "end": v(47.5, 4.44) * mm});
            skLineSegment(sketch, "E437", {"start": v(47.5, 4.44) * mm, "end": v(50.15, 5.97) * mm});
            skLineSegment(sketch, "E438", {"start": v(50.15, 5.97) * mm, "end": v(50.15, 9.03) * mm});
            skLineSegment(sketch, "E439", {"start": v(50.15, 9.03) * mm, "end": v(47.5, 10.56) * mm});
            skLineSegment(sketch, "E440", {"start": v(14.5, -73.5) * mm, "end": v(-11.5, -73.5) * mm});
            skLineSegment(sketch, "E441", {"start": v(24.5, -73.5) * mm, "end": v(20.5, -73.5) * mm});
            skLineSegment(sketch, "E442", {"start": v(-21.5, -73.5) * mm, "end": v(-24.5, -73.5) * mm});
            skLineSegment(sketch, "E443", {"start": v(-113.5, 64.5) * mm, "end": v(-104.5, 73.5) * mm});
            skLineSegment(sketch, "E444", {"start": v(-55.5, 73.5) * mm, "end": v(-46.5, 64.5) * mm});
            skLineSegment(sketch, "E445", {"start": v(-33.5, 64.5) * mm, "end": v(-24.5, 73.5) * mm});
            skLineSegment(sketch, "E446", {"start": v(24.5, 73.5) * mm, "end": v(33.5, 64.5) * mm});
            skLineSegment(sketch, "E447", {"start": v(33.5, 15.5) * mm, "end": v(24.5, 6.5) * mm});
            skLineSegment(sketch, "E448", {"start": v(-24.5, 6.5) * mm, "end": v(-33.5, 15.5) * mm});
            skLineSegment(sketch, "E449", {"start": v(-46.5, 15.5) * mm, "end": v(-55.5, 6.5) * mm});
            skLineSegment(sketch, "E450", {"start": v(-104.5, 6.5) * mm, "end": v(-113.5, 15.5) * mm});
            skLineSegment(sketch, "E451", {"start": v(-113.5, -15.5) * mm, "end": v(-104.5, -6.5) * mm});
            skLineSegment(sketch, "E452", {"start": v(-55.5, -6.5) * mm, "end": v(-46.5, -15.5) * mm});
            skLineSegment(sketch, "E453", {"start": v(-46.5, -64.5) * mm, "end": v(-55.5, -73.5) * mm});
            skLineSegment(sketch, "E454", {"start": v(-104.5, -73.5) * mm, "end": v(-113.5, -64.5) * mm});
            skLineSegment(sketch, "E455", {"start": v(-33.5, -15.5) * mm, "end": v(-24.5, -6.5) * mm});
            skLineSegment(sketch, "E456", {"start": v(24.5, -6.5) * mm, "end": v(33.5, -15.5) * mm});
            skLineSegment(sketch, "E457", {"start": v(33.5, -64.5) * mm, "end": v(24.5, -73.5) * mm});
            skLineSegment(sketch, "E458", {"start": v(-24.5, -73.5) * mm, "end": v(-33.5, -64.5) * mm});
            skLineSegment(sketch, "E459", {"start": v(-42.5, -2.5) * mm, "end": v(-42.5, -77.5) * mm});
            skLineSegment(sketch, "E460", {"start": v(-42.5, 77.5) * mm, "end": v(-42.5, 2.5) * mm});
            skLineSegment(sketch, "E461", {"start": v(-37.5, -2.5) * mm, "end": v(-37.5, -77.5) * mm});
            skLineSegment(sketch, "E462", {"start": v(-37.5, 77.5) * mm, "end": v(-37.5, 2.5) * mm});
            skLineSegment(sketch, "E463", {"start": v(37.5, 77.5) * mm, "end": v(37.5, 2.5) * mm});
            skLineSegment(sketch, "E464", {"start": v(37.5, -2.5) * mm, "end": v(37.5, -77.5) * mm});
            skLineSegment(sketch, "E465", {"start": v(42.5, -2.5) * mm, "end": v(42.5, -77.5) * mm});
            skLineSegment(sketch, "E466", {"start": v(42.5, 77.5) * mm, "end": v(42.5, 2.5) * mm});
            skLineSegment(sketch, "E467", {"start": v(117.5, -2.5) * mm, "end": v(117.5, -77.5) * mm});
            skLineSegment(sketch, "E468", {"start": v(117.5, 77.5) * mm, "end": v(117.5, 2.5) * mm});
            skLineSegment(sketch, "E469", {"start": v(14.5, -77.5) * mm, "end": v(-11.5, -77.5) * mm});
            skLineSegment(sketch, "E470", {"start": v(-101.5, -77.5) * mm, "end": v(-117.5, -77.5) * mm});
            skLineSegment(sketch, "E471", {"start": v(-117.5, -2.5) * mm, "end": v(-117.5, -77.5) * mm});
            skLineSegment(sketch, "E472", {"start": v(-117.5, 77.5) * mm, "end": v(-117.5, 2.5) * mm});
            skLineSegment(sketch, "E473", {"start": v(-117.5, 2.5) * mm, "end": v(-86, 2.5) * mm});
            skLineSegment(sketch, "E474", {"start": v(-111.07, 72.96) * mm, "end": v(-111.29, 73.38) * mm});
            skLineSegment(sketch, "E475", {"start": v(77.75, -39.38) * mm, "end": v(82.25, -39.38) * mm});
            skLineSegment(sketch, "E476", {"start": v(77.75, -40.62) * mm, "end": v(82.25, -40.62) * mm});
            skLineSegment(sketch, "E477", {"start": v(77.75, -40.62) * mm, "end": v(77.75, -39.38) * mm});
            skLineSegment(sketch, "E478", {"start": v(82.25, -40.62) * mm, "end": v(82.25, -39.38) * mm});
            skLineSegment(sketch, "E479", {"start": v(14.5, -73.5) * mm, "end": v(14.5, -77.5) * mm});
            skLineSegment(sketch, "E480", {"start": v(20.5, -73.5) * mm, "end": v(20.5, -77.5) * mm});
            skLineSegment(sketch, "E481", {"start": v(-101.5, -73.5) * mm, "end": v(-101.5, -77.5) * mm});
            skLineSegment(sketch, "E482", {"start": v(-91.5, -73.5) * mm, "end": v(-91.5, -77.5) * mm});
            skLineSegment(sketch, "E483", {"start": v(-21.5, -73.5) * mm, "end": v(-21.5, -77.5) * mm});
            skLineSegment(sketch, "E484", {"start": v(-11.5, -73.5) * mm, "end": v(-11.5, -77.5) * mm});
            skLineSegment(sketch, "E485", {"start": v(-86, -6.5) * mm, "end": v(-86, -2.5) * mm});
            skLineSegment(sketch, "E486", {"start": v(-86, 2.5) * mm, "end": v(-86, 6.5) * mm});
            skLineSegment(sketch, "E487", {"start": v(-74, -6.5) * mm, "end": v(-74, -2.5) * mm});
            skLineSegment(sketch, "E488", {"start": v(-74, 2.5) * mm, "end": v(-74, 6.5) * mm});
            skLineSegment(sketch, "E489", {"start": v(-91.5, -77.5) * mm, "end": v(-42.5, -77.5) * mm});
            skLineSegment(sketch, "E490", {"start": v(-74, 2.5) * mm, "end": v(-42.5, 2.5) * mm});
            skLineSegment(sketch, "E491", {"start": v(-117.5, 77.5) * mm, "end": v(-42.5, 77.5) * mm});
            skLineSegment(sketch, "E492", {"start": v(-74, -2.5) * mm, "end": v(-42.5, -2.5) * mm});
            skLineSegment(sketch, "E493", {"start": v(-117.5, -2.5) * mm, "end": v(-86, -2.5) * mm});
            skLineSegment(sketch, "E494", {"start": v(-37.5, 77.5) * mm, "end": v(37.5, 77.5) * mm});
            skLineSegment(sketch, "E495", {"start": v(37.5, 2.5) * mm, "end": v(-37.5, 2.5) * mm});
            skLineSegment(sketch, "E496", {"start": v(-11.5, -77.5) * mm, "end": v(14.5, -77.5) * mm});
            skLineSegment(sketch, "E497", {"start": v(-37.5, -77.5) * mm, "end": v(-21.5, -77.5) * mm});
            skLineSegment(sketch, "E498", {"start": v(20.5, -77.5) * mm, "end": v(37.5, -77.5) * mm});
            skLineSegment(sketch, "E499", {"start": v(24.5, 73.5) * mm, "end": v(-24.5, 73.5) * mm});
            skLineSegment(sketch, "E500", {"start": v(37.5, -2.5) * mm, "end": v(-37.5, -2.5) * mm});
            skLineSegment(sketch, "E501", {"start": v(42.5, 77.5) * mm, "end": v(117.5, 77.5) * mm});
            skLineSegment(sketch, "E502", {"start": v(117.5, 2.5) * mm, "end": v(42.5, 2.5) * mm});
            skLineSegment(sketch, "E503", {"start": v(42.5, -77.5) * mm, "end": v(117.5, -77.5) * mm});
            skLineSegment(sketch, "E504", {"start": v(42.5, -2.5) * mm, "end": v(117.5, -2.5) * mm});
            skSolve(sketch);
        }
        {
            var Q0;
            Q0=makeQuery(id+"F0.imprint","IMPRINT",FACE,{"disambiguationData":[TD([[makeQuery(id+"F0.imprint","IMPRINT",EDGE,{"derivedFrom":sQuery(id+"F0.wireOp",EDGE,"E0")}),-1.0]])]});
            var Q1;
            Q1=makeQuery(id+"F0.imprint","IMPRINT",FACE,{"disambiguationData":[TD([[makeQuery(id+"F0.imprint","IMPRINT",EDGE,{"derivedFrom":sQuery(id+"F0.wireOp",EDGE,"E84")}),-1.0]])]});
            var Q2;
            Q2=makeQuery(id+"F0.imprint","IMPRINT",FACE,{"disambiguationData":[TD([[makeQuery(id+"F0.imprint","IMPRINT",EDGE,{"derivedFrom":sQuery(id+"F0.wireOp",EDGE,"E416")}),-1.0]])]});
            var Q3;
            Q3=makeQuery(id+"F0.imprint","IMPRINT",FACE,{"disambiguationData":[TD([[makeQuery(id+"F0.imprint","IMPRINT",EDGE,{"derivedFrom":sQuery(id+"F0.wireOp",EDGE,"E336")}),-1.0]])]});
            var Q4;
            Q4=makeQuery(id+"F0.imprint","IMPRINT",FACE,{"disambiguationData":[TD([[makeQuery(id+"F0.imprint","IMPRINT",EDGE,{"derivedFrom":sQuery(id+"F0.wireOp",EDGE,"E253")}),-1.0]])]});
            var Q5;
            Q5=makeQuery(id+"F0.imprint","IMPRINT",FACE,{"disambiguationData":[TD([[makeQuery(id+"F0.imprint","IMPRINT",EDGE,{"derivedFrom":sQuery(id+"F0.wireOp",EDGE,"E167")}),-1.0]])]});
            var Q6;
            Q6=makeQuery(id+"F0.imprint","IMPRINT",FACE,{"disambiguationData":[TD([[makeQuery(id+"F0.imprint","IMPRINT",EDGE,{"derivedFrom":sQuery(id+"F0.wireOp",EDGE,"E187")}),-1.0]])]});
            var Q7;
            Q7=makeQuery(id+"F0.imprint","IMPRINT",FACE,{"disambiguationData":[TD([[makeQuery(id+"F0.imprint","IMPRINT",EDGE,{"derivedFrom":sQuery(id+"F0.wireOp",EDGE,"E440")}),1.0]])]});
            extrude(context, id + "F1", {"entities" : qUnion([Q0, Q1, Q2, Q3, Q4, Q5, Q6, Q7]), "depth" : 3 * mm, "offsetDistance" : 25 * mm});
        }
    });
